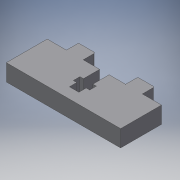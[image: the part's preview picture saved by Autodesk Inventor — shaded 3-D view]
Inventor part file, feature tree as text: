
AUTODESK INVENTOR PART (.ipt)
format: ipt  version: 2019 (Build 230136000, 136)  size: 165,888 bytes
history: native  units: in
note: dims shown in document units (in); Inventor stores cm internally (conversion verified against a paired STEP export)
features: extrude x3, sketch x3, other x2, fillet x1, reference x1, helix x1
ambient origin geometry x8: Origin, YZ Plane, XZ Plane, XY Plane, X Axis, Y Axis, Z Axis, Center Point
bodies: Solid1 (feature_tree)
feature tree (11):
  extrude  "Extrusion1"  Depth=0.2362in
  extrude  "Extrusion2"  Depth=0.0787in
  extrude  "Extrusion3"  Depth=0.0197in
  fillet  "Fillet1"  [1 undecoded]
  sketch  "Sketch1"  dims[d0=0.2362in d1=0.0in d2=0.0079in]
  reference  "Reference1"
  sketch  "Sketch2"  dims[d3=1.0in d4=0.0in d5=0.0787in]
  sketch  "Sketch3"  dims[d6=1.0in d7=0.0in d8=0.0197in]
  other  "<userpath>\Documents\CAD Files\Helix DLP\Helix DLP.iam"
  helix  "Helix DLP.iam"  [1 undecoded]
  other  "rod holder:1"
note: 2 required parameter values undecoded (feature->parameter linkage not recoverable at this tier; creation-order binding heuristic only, values carry confidence <= 0.55)
